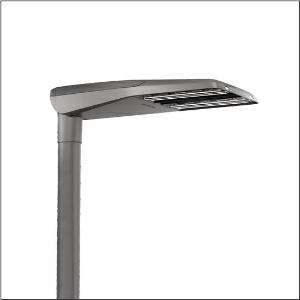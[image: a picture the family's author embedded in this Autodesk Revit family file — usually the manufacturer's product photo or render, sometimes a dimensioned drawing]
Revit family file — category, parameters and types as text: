
# Revit family: streetlight_sl_11_iq_midi___pc-r_5xc3f41f08me_b4e0
name_source: partatom
category: Lighting Fixtures
units: mm (PartAtom-declared; Revit-internal decimal feet)

## family parameters
Cut with Voids When Loaded = No
Host = Face
Light Source = No
Part Type = Normal
Room Calculation Point = No
Round Connector Dimension = Use Diameter
Shared = No

## types (1)
- --- (1 x LED, 16220 lm, 124.7 W, 4000K)
    Apparent Load = 125 VA
    CIE Flux Codes = 37 73 96 100 100
    Color Rendering = 70
    Color Temperature = 4000K
    Default Elevation = 1800 mm
    Description = Streetlight SL 11 iQ midi, mast luminaire, primary light control with 3 zone facetted reflector, of plastic, silver coated, highly specular, primary optical cover: cover, of PMMA, transparent, light distribution: PC-R, light emission: direct distribution, primary light characteristic: asymmetric, right, installation type: post-top, side-entry, LED, High Power LED, rated luminous flux: 16.220lm, luminous efficacy: 130lm/W, light colour: 740, colour temperature: 4000K, control: Street-Remote, optimised constant luminous flux control (CLO 2.0), Desk-Remote (wireless, voltage-free reading and setting of iQ features in the workshop via application-optimized NFC function/RFID function), Light-Fading, Smart-Wire, Night-Set, Lumen-Switch, Temp-Guard, Auto-Match, with cable H07RN-F 5x 1.5mm², mains connection: 230..240V, AC, 50/60Hz, connection cable pre-assembled, cable length: 12,5m, start of lifetime: 125W, end of service life: 132W, reduction: 57W, luminaire housing, of diecast aluminium, powder-coated, Siteco® metallic grey (DB 702S), please order mast flange separately, inclination adjustable without tools: 0°, 5°, 10°, 15° (post-top) | 0°, -5°, -10°, -15° (side-entry), sealing non-destructively replaceable, multi-level sealing system, length: 780mm, width: 376mm, height: 118mm, mast flange for spigot size: 42mm (side-entry): 5XC10008XM4, 60/48mm (side-entry/post-top): 5XC10108XM2, 76/60mm (side-entry/post-top): 5XC10108XM1, equipment: Power, protection rating (complete): IP66, insulation class (complete): insulation class II (safety insulation), certification: CE, ENEC, VDE, impact resistance: IK09, permissible operating ambient temperature for outdoor applications: -25..+50°C, standard-compliant lighting for roads and squares, Environmental Product Declaration (EPD) tested and certified by an independent institute, packaging unit: 1 piece

Light Distribution: PC-R
    Height = 118 mm
    Lamp = 1 x LED
    Lamp Light Flux = 16220 lm
    Lamp Power = 124.7 W
    Lamp count = 1
    Length = 780 mm
    Luminous efficacy = 130 lm/W
    Manufacturer = Siteco
    ModVariant = No
    Model = 5XC3F41F08ME
    Number of Poles = 1
    OnlyDefault = Yes
    Power Factor = 1
    Product Name = Streetlight SL 11 iQ midi | PC-R
    Product group = mast luminaire | pylon top
    ProductGroupID = 6100
    Protection Class = Protection class II
    Protection Degree = IP 66
    RLX_Detail_Level = 1
    RLX_Emergency_Light_Flux = 0 lm
    RLX_Emergency_Type = 0
    RLX_Emergency_Type_DB = No
    RlxData = <blob elided: 74461 chars, md5=b26cbdbe>
    Socket = socket
    Standby Power = 0 W
    System Light Flux = 16220 lm
    System Power = 125 W
    Type Comments = factory setting: luminous flux: 100 % | dim-lin: 254 | 557 mA
    Type Image = l_1005960.jpg
    URL = http://relux.com
    VarID = @adj_168653
    Voltage = 0 V
    Weight = 0.00 kg
    Width = 376 mm

## geometry (parser evidence)
native form markers: Blend x4, Sweep x11
no freeform markers — native parametric forms only
